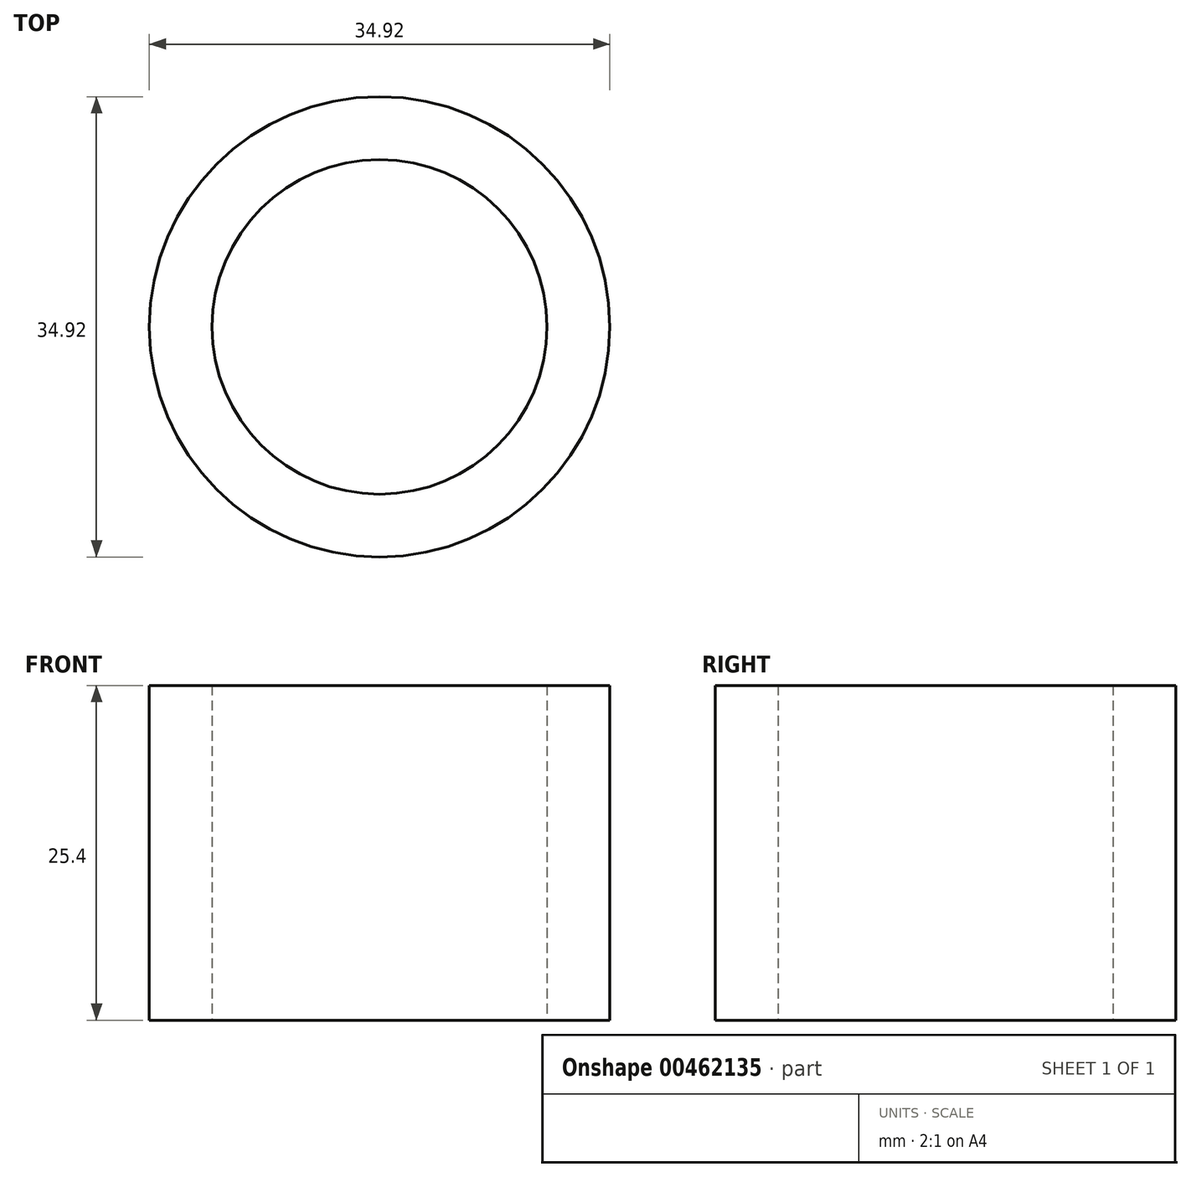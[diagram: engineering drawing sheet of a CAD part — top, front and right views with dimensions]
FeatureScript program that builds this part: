
annotation { "Feature Type Name" : "Feature", "Feature Type Description" : "" }
export const myFeature = defineFeature(function(context is Context, id is Id, definition is map)
    precondition{}
    {
        {
            var Q0;
            Q0=qCreatedBy(makeId("Top.planeOp"),FACE);
            var sketch = newSketch(context, id + "F0", { "sketchPlane" : qUnion([Q0])});
            skCircle(sketch, "E0", {"center": v(0, 0) * mm, "radius": 12.7 * mm});
            skCircle(sketch, "E1.0", {"center": v(0, 0) * mm, "radius": 17.46 * mm});
            skSolve(sketch);
        }
        {
            var Q0;
            Q0 = qSketchRegion(id + "F0", true);
            extrude(context, id + "F1", {"entities" : qUnion([Q0]), "depth" : 25.4 * mm});
        }
    });
